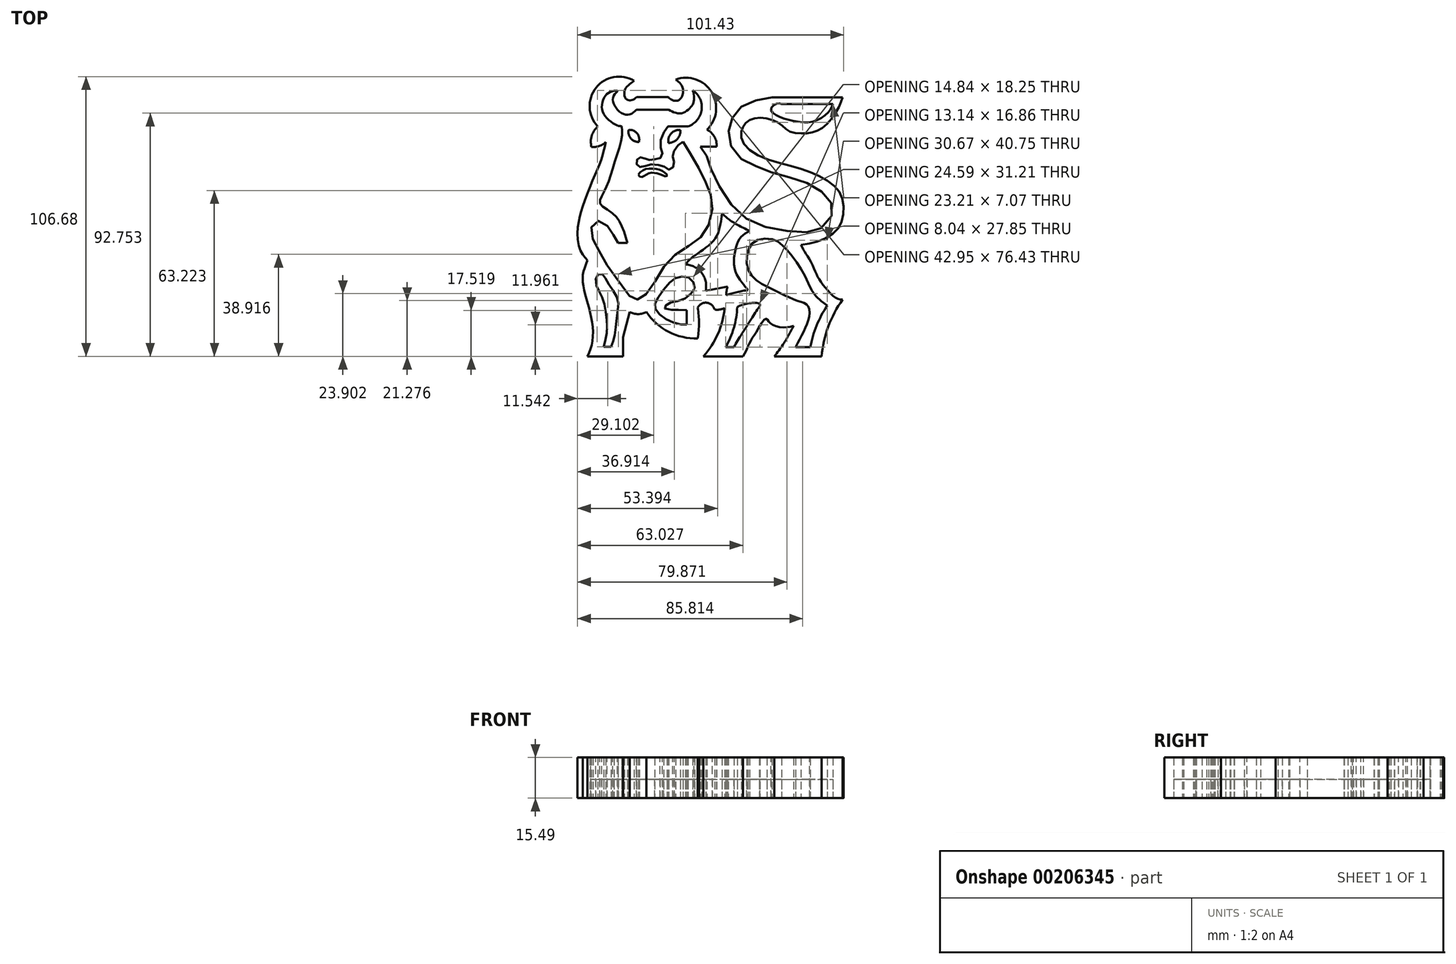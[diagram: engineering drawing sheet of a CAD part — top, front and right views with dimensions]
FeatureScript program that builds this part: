
annotation { "Feature Type Name" : "Feature", "Feature Type Description" : "" }
export const myFeature = defineFeature(function(context is Context, id is Id, definition is map)
    precondition{}
    {
        {
            var Q0;
            Q0=qCreatedBy(makeId("Top.planeOp"),FACE);
            var sketch = newSketch(context, id + "F0", { "sketchPlane" : qUnion([Q0])});
            skArc(sketch, "E0", {"start": v(0, 50.6) * mm, "mid": v(-14.53, 47.9) * mm, "end": v(-13.83, 33.12) * mm});
            skArc(sketch, "E1", {"start": v(-13.83, 33.12) * mm, "mid": v(-16.2, 29.6) * mm, "end": v(-16.22, 25.33) * mm});
            skArc(sketch, "E2", {"start": v(-16.22, 25.33) * mm, "mid": v(-13.3, 25.7) * mm, "end": v(-10.76, 27.2) * mm});
            skFitSpline(sketch, "E3", {"points": [v(-10.76, 27.2) * mm, v(-11.81, 22.97) * mm, v(-12.99, 19.34) * mm, v(-14.98, 14.53) * mm, v(-18.5, 5.97) * mm, v(-20.38, 0) * mm, v(-21.43, -5.17) * mm, v(-21.2, -11.97) * mm, v(-19.44, -15.96) * mm, v(-17.8, -17.84) * mm], "startDerivative": vector(-10.07, -42.36) * mm, "endDerivative": vector(21.49, -21.78) * mm});
            skFitSpline(sketch, "E4", {"points": [v(-17.8, -17.84) * mm, v(-19.44, -22.87) * mm, v(-19.44, -27.35) * mm, v(-17.8, -34) * mm, v(-16, -41.74) * mm, v(-16, -49.32) * mm, v(-17.8, -54.52) * mm], "startDerivative": vector(-13.03, -33.36) * mm, "endDerivative": vector(-13.75, -31.16) * mm});
            skLineSegment(sketch, "E5", {"start": v(-17.8, -54.52) * mm, "end": v(-4.23, -54.52) * mm});
            skLineSegment(sketch, "E6", {"start": v(-4.23, -54.52) * mm, "end": v(-4.23, -47.19) * mm});
            skLineSegment(sketch, "E7", {"start": v(-4.23, -47.19) * mm, "end": v(-1.68, -37.58) * mm});
            skArc(sketch, "E8", {"start": v(-1.68, -37.58) * mm, "mid": v(1.52, -38.39) * mm, "end": v(4.72, -37.58) * mm});
            skArc(sketch, "E9", {"start": v(4.72, -37.58) * mm, "mid": v(13.17, -45.18) * mm, "end": v(24.25, -47.67) * mm});
            skArc(sketch, "E10", {"start": v(24.25, -47.67) * mm, "mid": v(24.72, -41.82) * mm, "end": v(24.25, -35.98) * mm});
            skArc(sketch, "E11", {"start": v(30.65, -36.68) * mm, "mid": v(27.7, -34.06) * mm, "end": v(24.25, -35.98) * mm});
            skArc(sketch, "E12", {"start": v(30.65, -36.68) * mm, "mid": v(32.65, -36.67) * mm, "end": v(34.57, -36.08) * mm});
            skArc(sketch, "E13", {"start": v(26.41, -54.52) * mm, "mid": v(31.93, -45.94) * mm, "end": v(34.57, -36.08) * mm});
            skLineSegment(sketch, "E14", {"start": v(26.41, -54.52) * mm, "end": v(41.54, -54.52) * mm});
            skFitSpline(sketch, "E15", {"points": [v(41.54, -54.52) * mm, v(42.73, -52.26) * mm, v(43.56, -50.44) * mm, v(44.89, -47.8) * mm, v(46.63, -45.08) * mm, v(49.9, -40.27) * mm, v(50.89, -40.54) * mm, v(51.51, -41.52) * mm, v(53.67, -42.91) * mm, v(57.58, -43.47) * mm, v(60.86, -42.91) * mm], "startDerivative": vector(13.8, 25.66) * mm, "endDerivative": vector(30.11, 7.25) * mm});
            skFitSpline(sketch, "E16", {"points": [v(60.86, -42.91) * mm, v(59.03, -46.12) * mm, v(57.07, -49.57) * mm, v(53.44, -54.52) * mm], "startDerivative": vector(-6.22, -10.65) * mm, "endDerivative": vector(-10.26, -13.23) * mm});
            skLineSegment(sketch, "E17", {"start": v(53.44, -54.52) * mm, "end": v(71.47, -54.52) * mm});
            skArc(sketch, "E18", {"start": v(79.53, -32.9) * mm, "mid": v(74, -43.15) * mm, "end": v(71.47, -54.52) * mm});
            skFitSpline(sketch, "E19", {"points": [v(63.63, -12.05) * mm, v(70.71, -10.48) * mm, v(77.16, -6.42) * mm, v(79.53, -1.64) * mm, v(79.53, 4.81) * mm, v(76.92, 9.83) * mm, v(70.23, 14.37) * mm, v(60.8, 17.84) * mm, v(47.65, 21.9) * mm, v(41.44, 27.15) * mm, v(40.84, 31.22) * mm], "startDerivative": vector(71.55, 10.45) * mm, "endDerivative": vector(1.25, 54.65) * mm});
            skFitSpline(sketch, "E20", {"points": [v(40.84, 31.22) * mm, v(42.5, 34.54) * mm, v(46.14, 36.3) * mm, v(51.64, 35.97) * mm, v(56.37, 33.55) * mm, v(59.45, 31.22) * mm, v(64.56, 30.51) * mm, v(68.97, 31.22) * mm, v(73.38, 33.93) * mm, v(77.84, 40.15) * mm, v(79.53, 44.22) * mm], "startDerivative": vector(14.46, 41.79) * mm, "endDerivative": vector(13.99, 39.9) * mm});
            skLineSegment(sketch, "E21", {"start": v(79.53, 44.22) * mm, "end": v(52.53, 44.22) * mm});
            skFitSpline(sketch, "E22", {"points": [v(52.53, 44.22) * mm, v(45.31, 42.78) * mm, v(39.28, 39.37) * mm, v(36.65, 34.38) * mm, v(36, 29.26) * mm, v(39.15, 22.18) * mm, v(45.31, 18.5) * mm, v(52.53, 15.62) * mm, v(62.36, 12.87) * mm, v(70.1, 9.33) * mm, v(74.83, 4.6) * mm, v(75.61, 0) * mm, v(71.02, -5.76) * mm, v(64.99, -7.2) * mm, v(52.53, -5.76) * mm, v(41.38, -1.04) * mm, v(33.38, 8.8) * mm, v(28.92, 18.12) * mm, v(27.34, 22.44) * mm, v(25.24, 25.46) * mm], "startDerivative": vector(-139.82, -20.1) * mm, "endDerivative": vector(-63.2, 78.66) * mm});
            skLineSegment(sketch, "E23", {"start": v(25.24, 25.46) * mm, "end": v(31.4, 25.46) * mm});
            skArc(sketch, "E24", {"start": v(31.4, 25.46) * mm, "mid": v(30.6, 29.26) * mm, "end": v(27.74, 31.89) * mm});
            skArc(sketch, "E25", {"start": v(27.74, 31.89) * mm, "mid": v(29.53, 46.3) * mm, "end": v(15.8, 51.04) * mm});
            skFitSpline(sketch, "E26", {"points": [v(15.8, 51.04) * mm, v(17.9, 49.2) * mm, v(18.68, 46.19) * mm, v(17.5, 43.56) * mm, v(15.8, 42.9) * mm, v(14.1, 43.43) * mm, v(13.04, 44.35) * mm], "startDerivative": vector(12.58, -8.52) * mm, "endDerivative": vector(-7.15, 7.49) * mm});
            skLineSegment(sketch, "E27", {"start": v(13.04, 44.35) * mm, "end": v(0.98, 44.35) * mm});
            skFitSpline(sketch, "E28", {"points": [v(0.98, 44.35) * mm, v(-0.52, 43.31) * mm, v(-1.94, 43.11) * mm, v(-3.28, 43.85) * mm, v(-3.75, 45.8) * mm, v(-3.15, 47.88) * mm, v(-1, 49.83) * mm, v(0, 50.6) * mm], "startDerivative": vector(-10.4, -8.5) * mm, "endDerivative": vector(7.23, 5.74) * mm});
            skFitSpline(sketch, "E29", {"points": [v(79.53, -32.9) * mm, v(76.97, -32.26) * mm, v(73.36, -28.85) * mm, v(70.4, -24.91) * mm, v(68.9, -21.7) * mm, v(66.6, -17.03) * mm, v(64.89, -14.4) * mm, v(63.63, -12.05) * mm], "startDerivative": vector(-21.26, 2.05) * mm, "endDerivative": vector(-9.98, 20.04) * mm});
            skFitSpline(sketch, "E30", {"points": [v(-7.66, 46.75) * mm, v(-10.58, 45.38) * mm, v(-12.3, 41.26) * mm, v(-10.92, 36.97) * mm, v(-6.8, 33.7) * mm, v(-4.74, 33.19) * mm], "startDerivative": vector(-17.13, -4.7) * mm, "endDerivative": vector(12.56, -1.54) * mm});
            skFitSpline(sketch, "E31", {"points": [v(-4.74, 33.19) * mm, v(-4.74, 28.73) * mm, v(-7.49, 19.28) * mm, v(-10.23, 10.87) * mm, v(-12.64, 5.9) * mm, v(-12.8, 3.5) * mm, v(-8.17, 0) * mm, v(-4.74, -4.75) * mm, v(-2.5, -11.27) * mm], "startDerivative": vector(3.8, -37.49) * mm, "endDerivative": vector(15.16, -50.73) * mm});
            skFitSpline(sketch, "E32", {"points": [v(-2.5, -11.27) * mm, v(-6.11, -11.27) * mm], "startDerivative": vector(-3.6, 0) * mm, "endDerivative": vector(-3.6, 0) * mm});
            skFitSpline(sketch, "E33", {"points": [v(-6.11, -11.27) * mm, v(-7.49, -8.87) * mm, v(-9.2, -5.95) * mm, v(-12.3, -3.2) * mm, v(-14.87, -3.2) * mm, v(-16.58, -6.8) * mm, v(-14.87, -11.27) * mm, v(-11.6, -17.62) * mm, v(-4.91, -27.24) * mm, v(0, -33.07) * mm, v(1.75, -32.59) * mm, v(5.22, -30.15) * mm, v(9.85, -22.6) * mm, v(15.52, -15.9) * mm, v(22.55, -11.27) * mm, v(27.36, -6.64) * mm, v(29.76, 1.43) * mm, v(28.9, 7.95) * mm, v(26.5, 13.62) * mm, v(22.21, 21.52) * mm, v(18.6, 27.35) * mm], "startDerivative": vector(-40.48, 68.55) * mm, "endDerivative": vector(-64.9, 101.9) * mm});
            skFitSpline(sketch, "E34", {"points": [v(18.6, 27.35) * mm, v(16.55, 25.75) * mm, v(15, 23.26) * mm, v(14.69, 21.3) * mm, v(15.3, 19.01) * mm, v(14.48, 17.25) * mm, v(13.03, 16.73) * mm, v(11.58, 17.77) * mm, v(8.99, 18.5) * mm, v(5.78, 18.6) * mm, v(3.3, 17.77) * mm, v(1.75, 17.77) * mm, v(1, 18.75) * mm, v(1, 20.27) * mm, v(1.75, 21.26) * mm, v(3.69, 21.26) * mm, v(4.91, 20.44) * mm, v(6.32, 20.5) * mm, v(8.37, 20.68) * mm, v(10.36, 21.44) * mm, v(10.77, 23.28) * mm, v(9.95, 25.75) * mm, v(10.97, 30.25) * mm, v(12.92, 33.19) * mm], "startDerivative": vector(-44.93, -29.1) * mm, "endDerivative": vector(36.77, 46.76) * mm});
            skLineSegment(sketch, "E35", {"start": v(12.92, 33.19) * mm, "end": v(20.53, 33.19) * mm});
            skArc(sketch, "E36", {"start": v(20.53, 33.19) * mm, "mid": v(25.73, 39.47) * mm, "end": v(22.39, 46.92) * mm});
            skFitSpline(sketch, "E37", {"points": [v(22.39, 46.92) * mm, v(22.85, 44.15) * mm, v(22.39, 41.64) * mm, v(21.1, 40.05) * mm, v(18.84, 38.4) * mm, v(15.84, 38.36) * mm, v(13.19, 39.56) * mm], "startDerivative": vector(3.85, -16.05) * mm, "endDerivative": vector(-14.6, 8.18) * mm});
            skFitSpline(sketch, "E38", {"points": [v(13.19, 39.56) * mm, v(0.85, 39.56) * mm], "startDerivative": vector(-12.34, 0) * mm, "endDerivative": vector(-12.34, 0) * mm});
            skFitSpline(sketch, "E39", {"points": [v(0.85, 39.56) * mm, v(-1.15, 37.93) * mm, v(-3.86, 37.78) * mm, v(-6.87, 40.17) * mm, v(-8.1, 43.11) * mm, v(-7.4, 45.5) * mm, v(-6.33, 46.75) * mm, v(-7.66, 46.75) * mm], "startDerivative": vector(-12.6, -13.03) * mm, "endDerivative": vector(-18.37, -2.38) * mm});
            skLineSegment(sketch, "E40", {"start": v(-11.65, -50.93) * mm, "end": v(-8.73, -50.93) * mm});
            skFitSpline(sketch, "E41", {"points": [v(-8.73, -50.93) * mm, v(-7.48, -46.62) * mm, v(-6.37, -38.13) * mm, v(-6.37, -32.43) * mm, v(-9.84, -26.73) * mm, v(-12.1, -23.26) * mm, v(-14.15, -23.68) * mm, v(-14.3, -27.7) * mm, v(-12.1, -32.3) * mm, v(-10.54, -39.66) * mm, v(-10.4, -45.09) * mm, v(-11.65, -50.93) * mm], "startDerivative": vector(16.16, 45.62) * mm, "endDerivative": vector(-16.3, -61.82) * mm});
            skLineSegment(sketch, "E42", {"start": v(19.98, -36.93) * mm, "end": v(19.98, -42.37) * mm});
            skFitSpline(sketch, "E43", {"points": [v(19.98, -42.37) * mm, v(18.17, -42.37) * mm, v(14.42, -41.4) * mm, v(10.8, -39.4) * mm, v(8.27, -36.81) * mm, v(7.9, -34.88) * mm, v(8.93, -32.46) * mm, v(12.2, -27.94) * mm, v(15.15, -25.04) * mm, v(17.87, -24.07) * mm, v(20.89, -24.55) * mm, v(22.76, -26.55) * mm, v(23, -28.72) * mm, v(21.19, -31.02) * mm, v(17.75, -33.19) * mm, v(14.24, -33.91) * mm, v(12.43, -34.88) * mm, v(11.28, -35.97) * mm, v(13.28, -36.63) * mm, v(15.87, -36.81) * mm, v(19.98, -36.93) * mm], "startDerivative": vector(-42.22, -2.98) * mm, "endDerivative": vector(75.64, -2.17) * mm});
            skArc(sketch, "E44", {"start": v(34.87, -50.99) * mm, "mid": v(38.03, -43.57) * mm, "end": v(39.3, -35.61) * mm});
            skLineSegment(sketch, "E45", {"start": v(34.87, -50.99) * mm, "end": v(38.05, -50.99) * mm});
            skFitSpline(sketch, "E46", {"points": [v(39.3, -35.61) * mm, v(43.32, -34.37) * mm, v(47.89, -34.5) * mm, v(47.75, -35.61) * mm], "startDerivative": vector(8.96, 3.67) * mm, "endDerivative": vector(-2.88, -6.27) * mm});
            skFitSpline(sketch, "E47", {"points": [v(47.75, -35.61) * mm, v(45.04, -39.7) * mm, v(40.86, -46.26) * mm, v(38.05, -50.99) * mm], "startDerivative": vector(-8.38, -12.49) * mm, "endDerivative": vector(-8.1, -13.94) * mm});
            skFitSpline(sketch, "E48", {"points": [v(52.75, -34.37) * mm, v(52.75, -36.9) * mm, v(54.14, -38.8) * mm, v(56.82, -39.2) * mm, v(59.5, -38.7) * mm, v(60.86, -37.8) * mm], "startDerivative": vector(-1.54, -12.55) * mm, "endDerivative": vector(7.23, 6) * mm});
            skFitSpline(sketch, "E49", {"points": [v(60.6, -37.8) * mm, v(59.3, -36.7) * mm, v(56.92, -35.61) * mm, v(52.75, -34.37) * mm], "startDerivative": vector(-4.54, 4.38) * mm, "endDerivative": vector(-10.6, 2.94) * mm});
            skFitSpline(sketch, "E50", {"points": [v(50.66, -27.94) * mm, v(46.58, -25.48) * mm, v(43.32, -21) * mm, v(43.32, -14.94) * mm, v(46.29, -10.47) * mm, v(52.75, -9.88) * mm, v(56.72, -12.26) * mm, v(60.86, -17.03) * mm, v(65.17, -23.89) * mm, v(68.55, -30.65) * mm, v(73.61, -35.2) * mm], "startDerivative": vector(-47.35, 23.95) * mm, "endDerivative": vector(53.06, -38.54) * mm});
            skFitSpline(sketch, "E51", {"points": [v(50.66, -27.94) * mm, v(55.72, -30.42) * mm, v(62.58, -33.45) * mm, v(66.14, -35.03) * mm, v(66.8, -38.73) * mm, v(64.82, -44.66) * mm, v(61.53, -51) * mm], "startDerivative": vector(28.54, -13.97) * mm, "endDerivative": vector(-18.33, -33.44) * mm});
            skLineSegment(sketch, "E52", {"start": v(61.53, -51) * mm, "end": v(67.2, -51) * mm});
            skArc(sketch, "E53", {"start": v(73.61, -35.2) * mm, "mid": v(69.58, -42.76) * mm, "end": v(67.2, -51) * mm});
            skArc(sketch, "E54", {"start": v(43.46, -29.23) * mm, "mid": v(39.25, -30) * mm, "end": v(35.15, -31.2) * mm});
            skArc(sketch, "E55", {"start": v(35.64, -27.83) * mm, "mid": v(35.27, -29.5) * mm, "end": v(35.15, -31.2) * mm});
            skLineSegment(sketch, "E56", {"start": v(35.64, -27.83) * mm, "end": v(27.28, -29.5) * mm});
            skPoint(sketch, "E56.endSnap0", {"position": v(35.27, -29.5) * mm});
            skArc(sketch, "E57", {"start": v(27.28, -29.5) * mm, "mid": v(25.73, -22.67) * mm, "end": v(19.5, -19.47) * mm});
            skFitSpline(sketch, "E58", {"points": [v(19.5, -19.47) * mm, v(21.44, -17.37) * mm, v(25.15, -14.64) * mm, v(30.72, -9.85) * mm, v(32.77, -4.77) * mm, v(33.55, 0) * mm], "startDerivative": vector(11.54, 13.92) * mm, "endDerivative": vector(3.33, 23.86) * mm});
            skFitSpline(sketch, "E59", {"points": [v(33.55, 0) * mm, v(35.7, -1.94) * mm, v(38.92, -4.09) * mm, v(44.1, -6.72) * mm], "startDerivative": vector(7.29, -7) * mm, "endDerivative": vector(13.79, -6.68) * mm});
            skFitSpline(sketch, "E60", {"points": [v(44.1, -6.72) * mm, v(40.58, -9.17) * mm, v(38.63, -13.76) * mm, v(38.34, -21.08) * mm, v(41.17, -26.45) * mm, v(43.46, -29.23) * mm], "startDerivative": vector(-21.43, -11.4) * mm, "endDerivative": vector(13.13, -15.18) * mm});
            skFitSpline(sketch, "E61", {"points": [v(1.64, 14.75) * mm, v(3.3, 16.39) * mm, v(5, 17) * mm, v(7.82, 17.04) * mm, v(10.12, 16.53) * mm, v(11.83, 15.5) * mm, v(12.54, 14.6) * mm, v(12.2, 14.08) * mm, v(11.18, 14.35) * mm, v(9.51, 15.08) * mm, v(7.9, 15.4) * mm, v(6.15, 15.44) * mm, v(4.6, 14.8) * mm, v(3.3, 14) * mm, v(2.44, 13.93) * mm, v(1.64, 14.75) * mm]});
            skArc(sketch, "E62", {"start": v(17.62, 31.83) * mm, "mid": v(14.1, 30.48) * mm, "end": v(13.1, 26.85) * mm});
            skArc(sketch, "E63", {"start": v(13.1, 26.85) * mm, "mid": v(16.44, 28.36) * mm, "end": v(17.62, 31.83) * mm});
            skArc(sketch, "E64", {"start": v(-2.11, 31.84) * mm, "mid": v(-1.24, 28.6) * mm, "end": v(1.82, 27.22) * mm});
            skArc(sketch, "E65", {"start": v(1.82, 27.22) * mm, "mid": v(1.08, 30.58) * mm, "end": v(-2.11, 31.84) * mm});
            skLineSegment(sketch, "E66", {"start": v(56.17, 41.77) * mm, "end": v(75.83, 41.77) * mm});
            skFitSpline(sketch, "E67", {"points": [v(56.17, 41.77) * mm, v(54.11, 41.77) * mm, v(52.21, 39.55) * mm, v(56.17, 36.54) * mm, v(61.88, 35.1) * mm, v(67.9, 34.95) * mm, v(73.93, 38.44) * mm, v(75.83, 41.77) * mm], "startDerivative": vector(-20.17, 4.5) * mm, "endDerivative": vector(10.13, 25.32) * mm});
            skSolve(sketch);
        }
        {
            var Q0;
            Q0=makeQuery(id+"F0.imprint","IMPRINT",FACE,{"disambiguationData":[TD([[makeQuery(id+"F0.imprint","IMPRINT",EDGE,{"derivedFrom":sQuery(id+"F0.wireOp",EDGE,"E0")}),1.0]])]});
            var Q1;
            Q1=makeQuery(id+"F0.imprint","IMPRINT",FACE,{"disambiguationData":[TD([[makeQuery(id+"F0.imprint","IMPRINT",EDGE,{"derivedFrom":sQuery(id+"F0.wireOp",EDGE,"E61")}),-1.0]])]});
            var Q2;
            Q2=makeQuery(id+"F0.imprint","IMPRINT",FACE,{"disambiguationData":[TD([[makeQuery(id+"F0.imprint","IMPRINT",EDGE,{"derivedFrom":sQuery(id+"F0.wireOp",EDGE,"E64")}),1.0]])]});
            extrude(context, id + "F1", {"entities" : qUnion([Q0, Q1, Q2]), "depth" : 15.5 * mm});
        }
        {
            var Q0;
            Q0=makeQuery(id+"F0.imprint","IMPRINT",FACE,{"disambiguationData":[TD([[makeQuery(id+"F0.imprint","IMPRINT",EDGE,{"derivedFrom":sQuery(id+"F0.wireOp",EDGE,"E30")}),1.0]])]});
            var Q1;
            Q1=makeQuery(id+"F0.imprint","IMPRINT",FACE,{"disambiguationData":[TD([[makeQuery(id+"F0.imprint","IMPRINT",EDGE,{"derivedFrom":sQuery(id+"F0.wireOp",EDGE,"E66")}),-1.0]])]});
            var Q2;
            Q2=makeQuery(id+"F0.imprint","IMPRINT",FACE,{"disambiguationData":[TD([[makeQuery(id+"F0.imprint","IMPRINT",EDGE,{"derivedFrom":sQuery(id+"F0.wireOp",EDGE,"E50")}),-1.0]])]});
            var Q3;
            Q3=makeQuery(id+"F0.imprint","IMPRINT",FACE,{"disambiguationData":[TD([[makeQuery(id+"F0.imprint","IMPRINT",EDGE,{"derivedFrom":sQuery(id+"F0.wireOp",EDGE,"E42")}),-1.0]])]});
            var Q4;
            Q4=makeQuery(id+"F0.imprint","IMPRINT",FACE,{"disambiguationData":[TD([[makeQuery(id+"F0.imprint","IMPRINT",EDGE,{"derivedFrom":sQuery(id+"F0.wireOp",EDGE,"E40")}),1.0]])]});
            var Q5;
            Q5=makeQuery(id+"F0.imprint","IMPRINT",FACE,{"disambiguationData":[TD([[makeQuery(id+"F0.imprint","IMPRINT",EDGE,{"derivedFrom":sQuery(id+"F0.wireOp",EDGE,"E44")}),-1.0]])]});
            var Q6;
            Q6=makeQuery(id+"F0.imprint","IMPRINT",FACE,{"disambiguationData":[TD([[makeQuery(id+"F0.imprint","IMPRINT",EDGE,{"derivedFrom":sQuery(id+"F0.wireOp",EDGE,"E54")}),-1.0]])]});
            var Q7;
            Q7=makeQuery(id+"F0.imprint","IMPRINT",FACE,{"disambiguationData":[TD([[makeQuery(id+"F0.imprint","IMPRINT",EDGE,{"derivedFrom":sQuery(id+"F0.wireOp",EDGE,"E62")}),1.0]])]});
            extrude(context, id + "F2", {"entities" : qUnion([Q0, Q1, Q2, Q3, Q4, Q5, Q6, Q7]), "depth" : 7.11 * mm});
        }
    });
